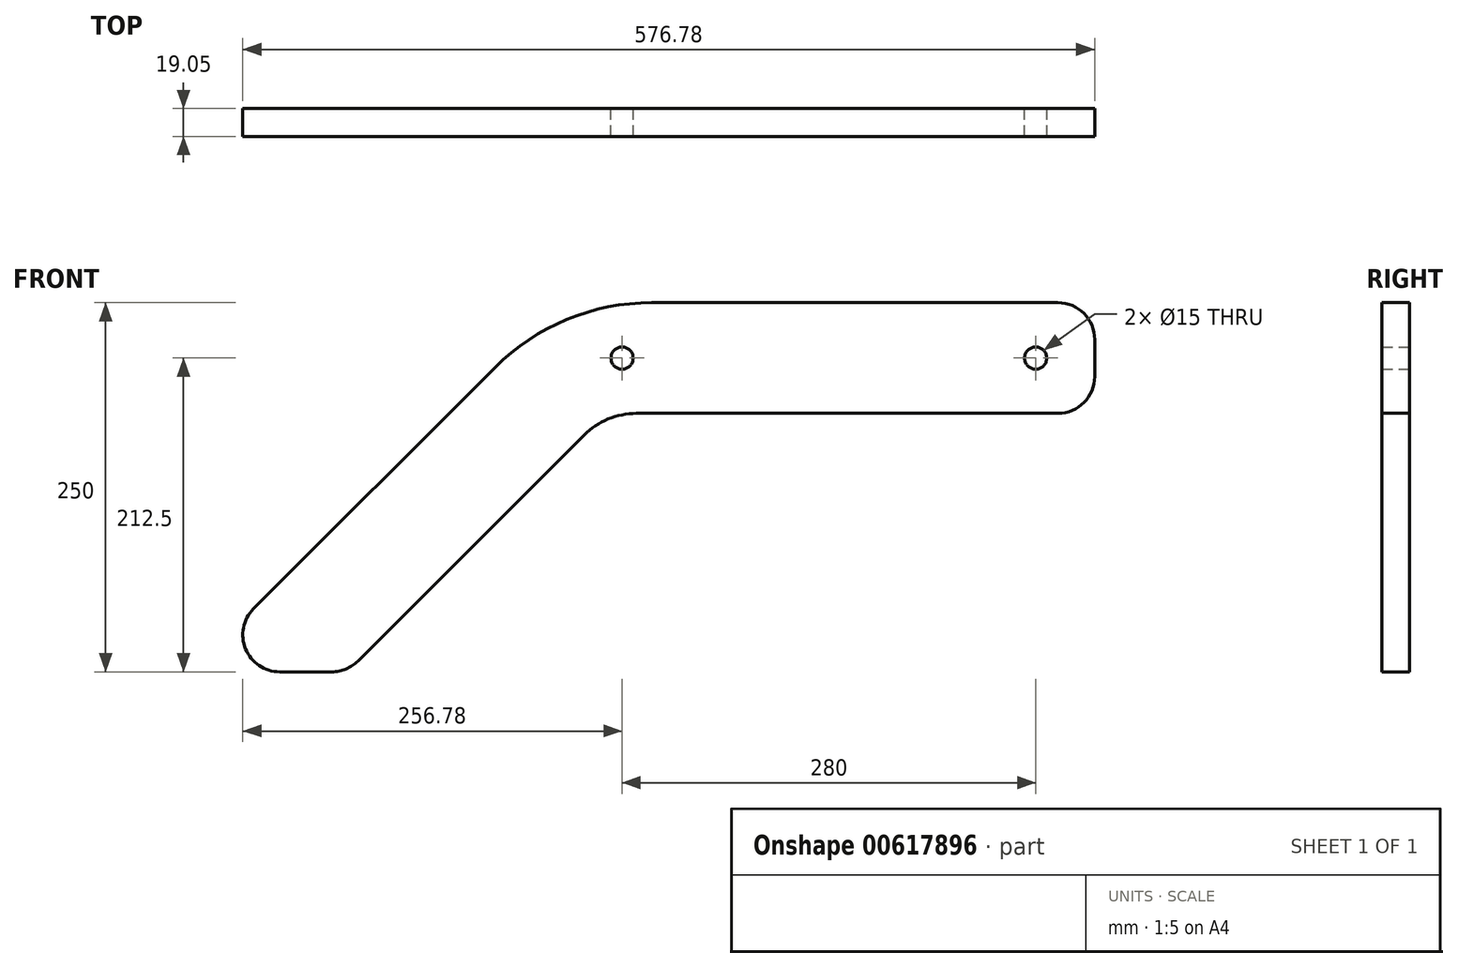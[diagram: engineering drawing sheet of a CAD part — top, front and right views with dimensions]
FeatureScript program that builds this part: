
annotation { "Feature Type Name" : "Feature", "Feature Type Description" : "" }
export const myFeature = defineFeature(function(context is Context, id is Id, definition is map)
    precondition{}
    {
        {
            var Q0;
            Q0=qCreatedBy(makeId("Front.planeOp"),FACE);
            var sketch = newSketch(context, id + "F0", { "sketchPlane" : qUnion([Q0])});
            skLineSegment(sketch, "E0", {"start": v(0, 25) * mm, "end": v(0, 50) * mm});
            skLineSegment(sketch, "E1", {"start": v(-25, 75) * mm, "end": v(-300, 75) * mm});
            skLineSegment(sketch, "E2", {"start": v(-406.07, 31.07) * mm, "end": v(-569.45, -132.32) * mm});
            skLineSegment(sketch, "E3", {"start": v(-551.78, -175) * mm, "end": v(-516.42, -175) * mm});
            skLineSegment(sketch, "E4", {"start": v(-498.74, -167.68) * mm, "end": v(-345.71, -14.64) * mm});
            skLineSegment(sketch, "E5", {"start": v(-310.36, 0) * mm, "end": v(-25, 0) * mm});
            skPoint(sketch, "E6.visualSharp", {"position": v(-362.13, 75) * mm});
            skArc(sketch, "E6.filletArc", {"start": v(-300, 75) * mm, "mid": v(-357.4, 63.58) * mm, "end": v(-406.07, 31.07) * mm});
            skPoint(sketch, "E7.visualSharp", {"position": v(-331.07, 0) * mm});
            skArc(sketch, "E7.filletArc", {"start": v(-310.36, 0) * mm, "mid": v(-329.49, -3.8) * mm, "end": v(-345.71, -14.64) * mm});
            skPoint(sketch, "E8.visualSharp", {"position": v(-612.13, -175) * mm});
            skArc(sketch, "E8.filletArc", {"start": v(-569.45, -132.32) * mm, "mid": v(-574.87, -159.57) * mm, "end": v(-551.78, -175) * mm});
            skPoint(sketch, "E9.visualSharp", {"position": v(-506.07, -175) * mm});
            skArc(sketch, "E9.filletArc", {"start": v(-516.42, -175) * mm, "mid": v(-506.85, -173.1) * mm, "end": v(-498.74, -167.68) * mm});
            skPoint(sketch, "E10.visualSharp", {"position": v(0, 75) * mm});
            skArc(sketch, "E10.filletArc", {"start": v(0, 50) * mm, "mid": v(-7.32, 67.68) * mm, "end": v(-25, 75) * mm});
            skPoint(sketch, "E11.visualSharp", {"position": v(0, 0) * mm});
            skArc(sketch, "E11.filletArc", {"start": v(-25, 0) * mm, "mid": v(-7.32, 7.32) * mm, "end": v(0, 25) * mm});
            skCircle(sketch, "E12", {"center": v(-40, 37.5) * mm, "radius": 7.5 * mm});
            skCircle(sketch, "E13", {"center": v(-320, 37.5) * mm, "radius": 7.5 * mm});
            skLineSegment(sketch, "E14", {"start": v(-320, 37.5) * mm, "end": v(-40, 37.5) * mm, "construction": true});
            skSolve(sketch);
        }
        {
            var Q0;
            Q0 = qSketchRegion(id + "F0", true);
            extrude(context, id + "F1", {"entities" : qUnion([Q0]), "depth" : (0.75 * 25.4) * mm, "offsetDistance" : 25 * mm});
        }
    });
